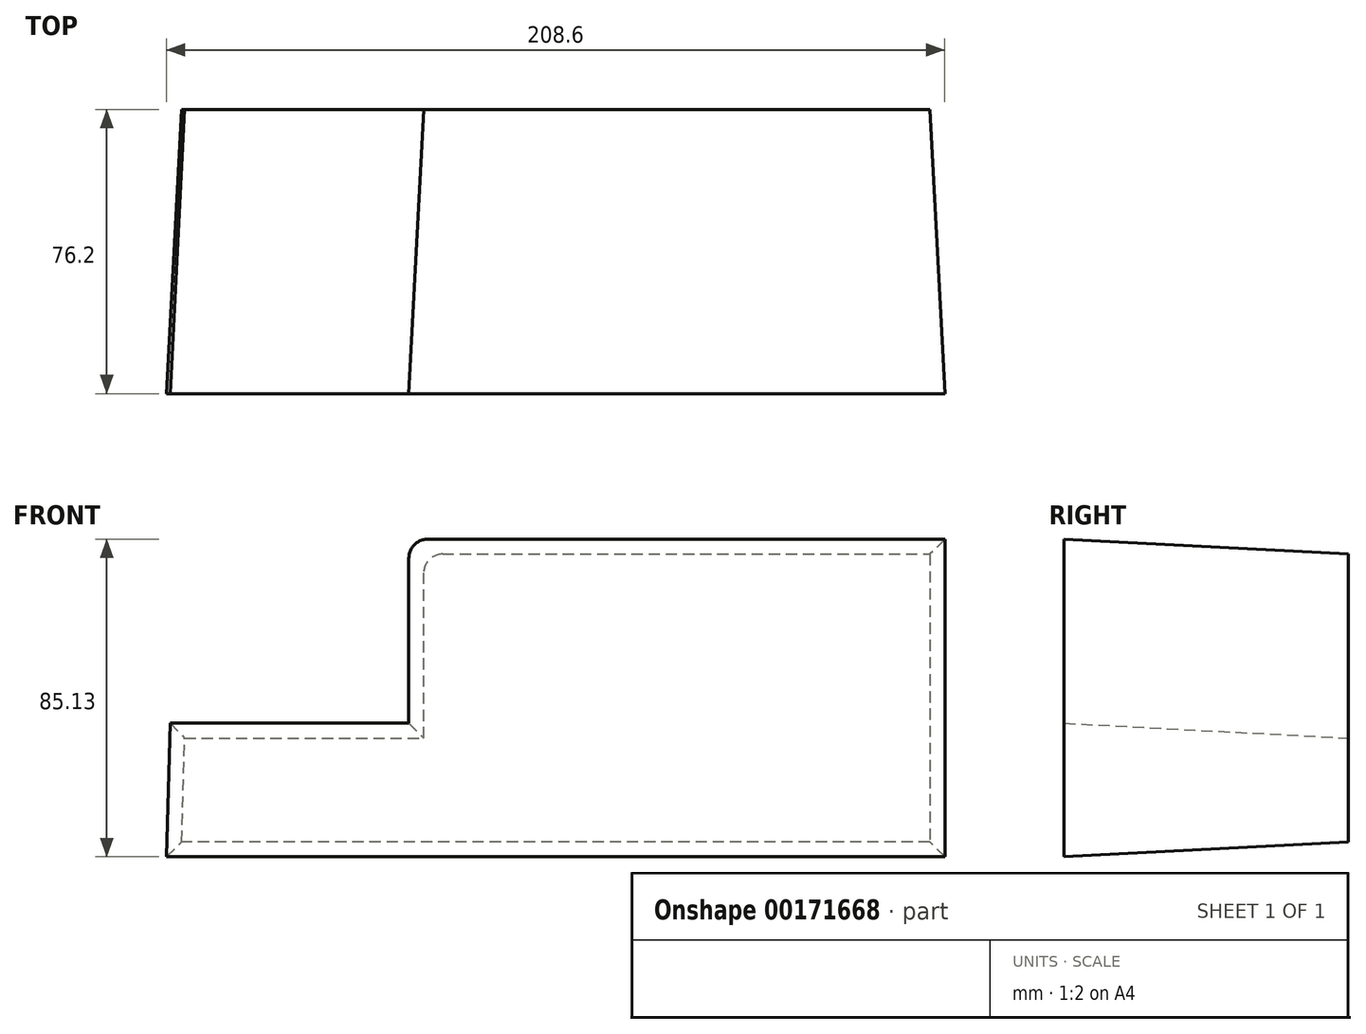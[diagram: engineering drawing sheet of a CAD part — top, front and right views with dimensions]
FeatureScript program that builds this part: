
annotation { "Feature Type Name" : "Feature", "Feature Type Description" : "" }
export const myFeature = defineFeature(function(context is Context, id is Id, definition is map)
    precondition{}
    {
        {
            var Q0;
            Q0=qCreatedBy(makeId("Front.planeOp"),FACE);
            var sketch = newSketch(context, id + "F0", { "sketchPlane" : qUnion([Q0])});
            skLineSegment(sketch, "E0", {"start": v(-114.41, -27.81) * mm, "end": v(86.1, -27.81) * mm});
            skLineSegment(sketch, "E1", {"start": v(86.1, -27.81) * mm, "end": v(86.1, 49.33) * mm});
            skLineSegment(sketch, "E2", {"start": v(86.1, 49.33) * mm, "end": v(-49.57, 49.33) * mm});
            skLineSegment(sketch, "E3", {"start": v(-49.57, 49.33) * mm, "end": v(-49.57, 0) * mm});
            skLineSegment(sketch, "E4", {"start": v(-49.57, 0) * mm, "end": v(-113.67, 0) * mm});
            skLineSegment(sketch, "E5", {"start": v(-113.67, 0) * mm, "end": v(-114.41, -27.81) * mm});
            skSolve(sketch);
        }
        {
            var Q0;
            Q0 = qSketchRegion(id + "F0", true);
            extrude(context, id + "F1", {"entities" : qUnion([Q0]), "depth" : 76.2 * mm, "hasDraft" : true, "draftAngle" : 3 * degree});
        }
        {
            var Q0;
            Q0=makeQuery(id+"F1.opExtrude","SWEPT_EDGE",EDGE,{"disambiguationData":[OSD([sQuery(id+"F0.wireOp",EDGE,"E2"),sQuery(id+"F0.wireOp",EDGE,"E3")])]});
            fillet(context, id + "F2", {"entities" : qUnion([Q0]), "radius" : 5.08 * mm, "tangentPropagation" : true, "allowEdgeOverflow" : false});
        }
    });
